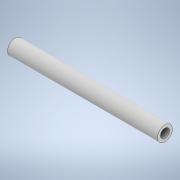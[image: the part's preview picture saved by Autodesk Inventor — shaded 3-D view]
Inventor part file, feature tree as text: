
AUTODESK INVENTOR PART (.ipt)
format: ipt  version: 2020 (Build 240168000, 168)  size: 97,792 bytes
history: native  units: mm
features: other x1, extrude x1, sketch x1
ambient origin geometry x8: Origin, YZ Plane, XZ Plane, XY Plane, X Axis, Y Axis, Z Axis, Center Point
bodies: Body1 (feature_tree)
feature tree (3):
  other  "Твердое тело1"
  extrude  "Выдавливание1"  Depth=3.0mm
  sketch  "Эскиз1"
